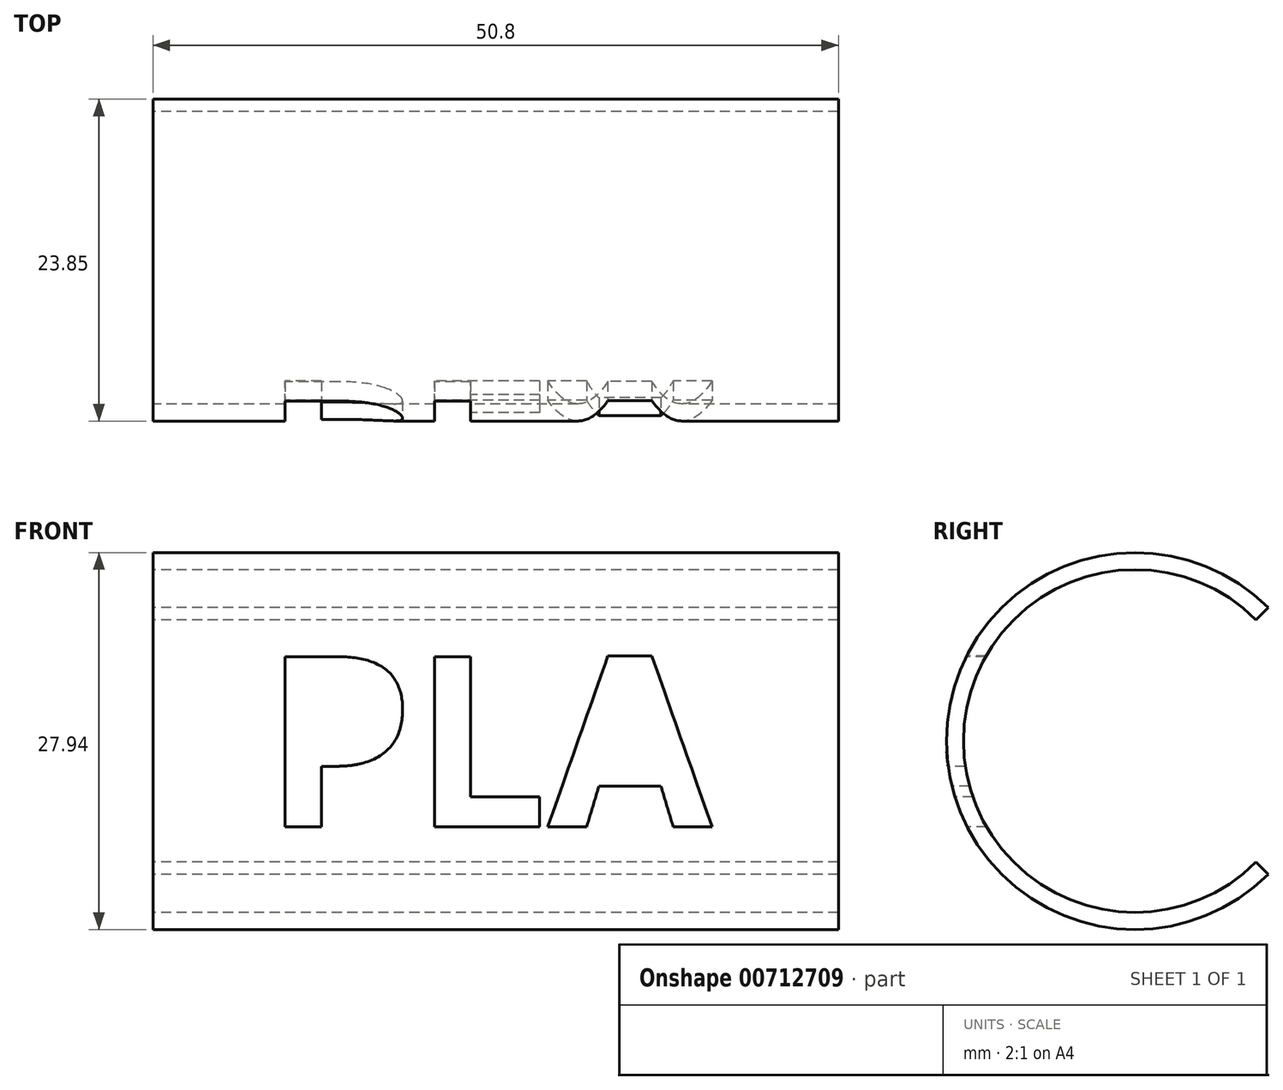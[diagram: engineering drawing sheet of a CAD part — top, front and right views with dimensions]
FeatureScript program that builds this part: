
annotation { "Feature Type Name" : "Feature", "Feature Type Description" : "" }
export const myFeature = defineFeature(function(context is Context, id is Id, definition is map)
    precondition{}
    {
        {
            var Q0;
            Q0=qCreatedBy(makeId("Right.planeOp"),FACE);
            var sketch = newSketch(context, id + "F0", { "sketchPlane" : qUnion([Q0])});
            skCircle(sketch, "E0", {"center": v(0, 0) * mm, "radius": 12.7 * mm});
            skCircle(sketch, "E1", {"center": v(0, 0) * mm, "radius": 13.97 * mm});
            skLineSegment(sketch, "E2", {"start": v(0, 0) * mm, "end": v(13.97, 0) * mm});
            skLineSegment(sketch, "E3", {"start": v(0, 0) * mm, "end": v(9.88, 9.88) * mm});
            skLineSegment(sketch, "E4.MirrorCS", {"start": v(0, 0) * mm, "end": v(9.88, -9.88) * mm});
            skSolve(sketch);
        }
        {
            var Q0;
            {var subQ0=sQuery(id+"F0.wireOp",EDGE,"E3");var subQ1=sQuery(id+"F0.wireOp",EDGE,"E0");var subQ2=makeQuery(id+"F0.imprint","INTERSECT",VERTEX,{"derivedFrom":[subQ1,subQ0]});Q0=makeQuery(id+"F0.imprint","IMPRINT",FACE,{"disambiguationData":[TD([[makeQuery(id+"F0.imprint","IMPRINT",EDGE,{"disambiguationData":[TD([[subQ2,-1.0]])],"derivedFrom":subQ1}),-1.0]])]});}
            extrude(context, id + "F1", {"entities" : qUnion([Q0]), "depth" : 50.8 * mm, "offsetDistance" : 25.4 * mm});
        }
        {
            var Q0;
            Q0=qCreatedBy(makeId("Front.planeOp"),FACE);
            cPlane(context, id + "F2", {"entities" : qUnion([Q0]), "cplaneType" : CPlaneType.OFFSET, "offset" : 25.4 * mm, "width" : 152.4 * mm, "height" : 152.4 * mm});
        }
        {
            var Q0;
            Q0=qCreatedBy(id+"F2.planeOp",FACE);
            var sketch = newSketch(context, id + "F3", { "sketchPlane" : qUnion([Q0])});
            skLineSegment(sketch, "E5.bottom", {"start": v(0, 13.97) * mm, "end": v(50.8, 13.97) * mm});
            skLineSegment(sketch, "E5.top", {"start": v(0, -13.97) * mm, "end": v(50.8, -13.97) * mm});
            skLineSegment(sketch, "E5.left", {"start": v(0, 13.97) * mm, "end": v(0, -13.97) * mm});
            skLineSegment(sketch, "E5.right", {"start": v(50.8, 13.97) * mm, "end": v(50.8, -13.97) * mm});
            skPoint(sketch, "E6", {"position": v(25.4, 13.97) * mm});
            skText(sketch, "E7", { "text": "PLA", "fontName": "OpenSans-Bold.ttf"});
            const initialGuessF3  = {"E7": [0.00822, -0.00635, 1, 0, 0.0127]};
            skSetInitialGuess(sketch, initialGuessF3);
            skSolve(sketch);
        }
        {
            var Q0;
            Q0=makeQuery(id+"F3.imprint","IMPRINT",FACE,{"disambiguationData":[TD([[makeQuery(id+"F3.imprint","IMPRINT",EDGE,{"derivedFrom":sQuery(id+"F3.wireOp",EDGE,"E7.sketch_text.stroke-30")}),1.0]])]});
            var Q1;
            Q1=makeQuery(id+"F3.imprint","IMPRINT",FACE,{"disambiguationData":[TD([[makeQuery(id+"F3.imprint","IMPRINT",EDGE,{"derivedFrom":sQuery(id+"F3.wireOp",EDGE,"E7.sketch_text.stroke-22")}),-1.0]])]});
            var Q2;
            Q2=makeQuery(id+"F3.imprint","IMPRINT",FACE,{"disambiguationData":[TD([[makeQuery(id+"F3.imprint","IMPRINT",EDGE,{"derivedFrom":sQuery(id+"F3.wireOp",EDGE,"E7.sketch_text.stroke-16")}),-1.0]])]});
            var Q3;
            Q3=makeQuery(id+"F3.imprint","IMPRINT",FACE,{"disambiguationData":[TD([[makeQuery(id+"F3.imprint","IMPRINT",EDGE,{"derivedFrom":sQuery(id+"F3.wireOp",EDGE,"E7.sketch_text.stroke-0")}),-1.0]])]});
            var Q4;
            Q4=makeQuery(id+"F3.imprint","IMPRINT",FACE,{"disambiguationData":[TD([[makeQuery(id+"F3.imprint","IMPRINT",EDGE,{"derivedFrom":sQuery(id+"F3.wireOp",EDGE,"E7.sketch_text.stroke-0")}),1.0]])]});
            extrude(context, id + "F4", {"entities" : qUnion([Q0, Q1, Q2, Q3, Q4]), "operationType" : NewBodyOperationType.REMOVE, "endBound" : BoundingType.THROUGH_ALL, "oppositeDirection" : true, "depth" : 25.4 * mm, "offsetDistance" : 25.4 * mm});
        }
    });
